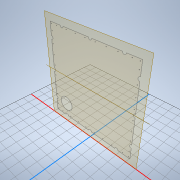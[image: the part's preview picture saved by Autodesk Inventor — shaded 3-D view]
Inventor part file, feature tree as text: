
AUTODESK INVENTOR PART (.ipt)
format: ipt  version: 2021 (Build 250183000, 183)  size: 234,496 bytes
history: native  units: mm
features: other x6, sketch x2, extrude x2, reference x1
ambient origin geometry x8: Origin, YZ Plane, XZ Plane, XY Plane, X Axis, Y Axis, Z Axis, Center Point
bodies: Body1 (feature_tree)
feature tree (11):
  other  "Bryła1"
  other  "Płaszczyzna konstrukcyjna1"
  sketch  "Szkic1"
  other  "Oś konstrukcyjna1"
  extrude  "Wyciągnięcie proste1"  Depth=875.0mm
  extrude  "Wyciągnięcie proste2"  Depth=35.0mm
  reference  "Odniesienie1"
  sketch  "Szkic2"
  parser-record x1  (decoder bookkeeping rows leaked as tree rows — omitted from the tree; the rows remain in map.json)
  other  "zespolokno.iam"
  other  "alu:1"
note: 1 file-system path scrubbed to <path> (originals preserved in map.json)
